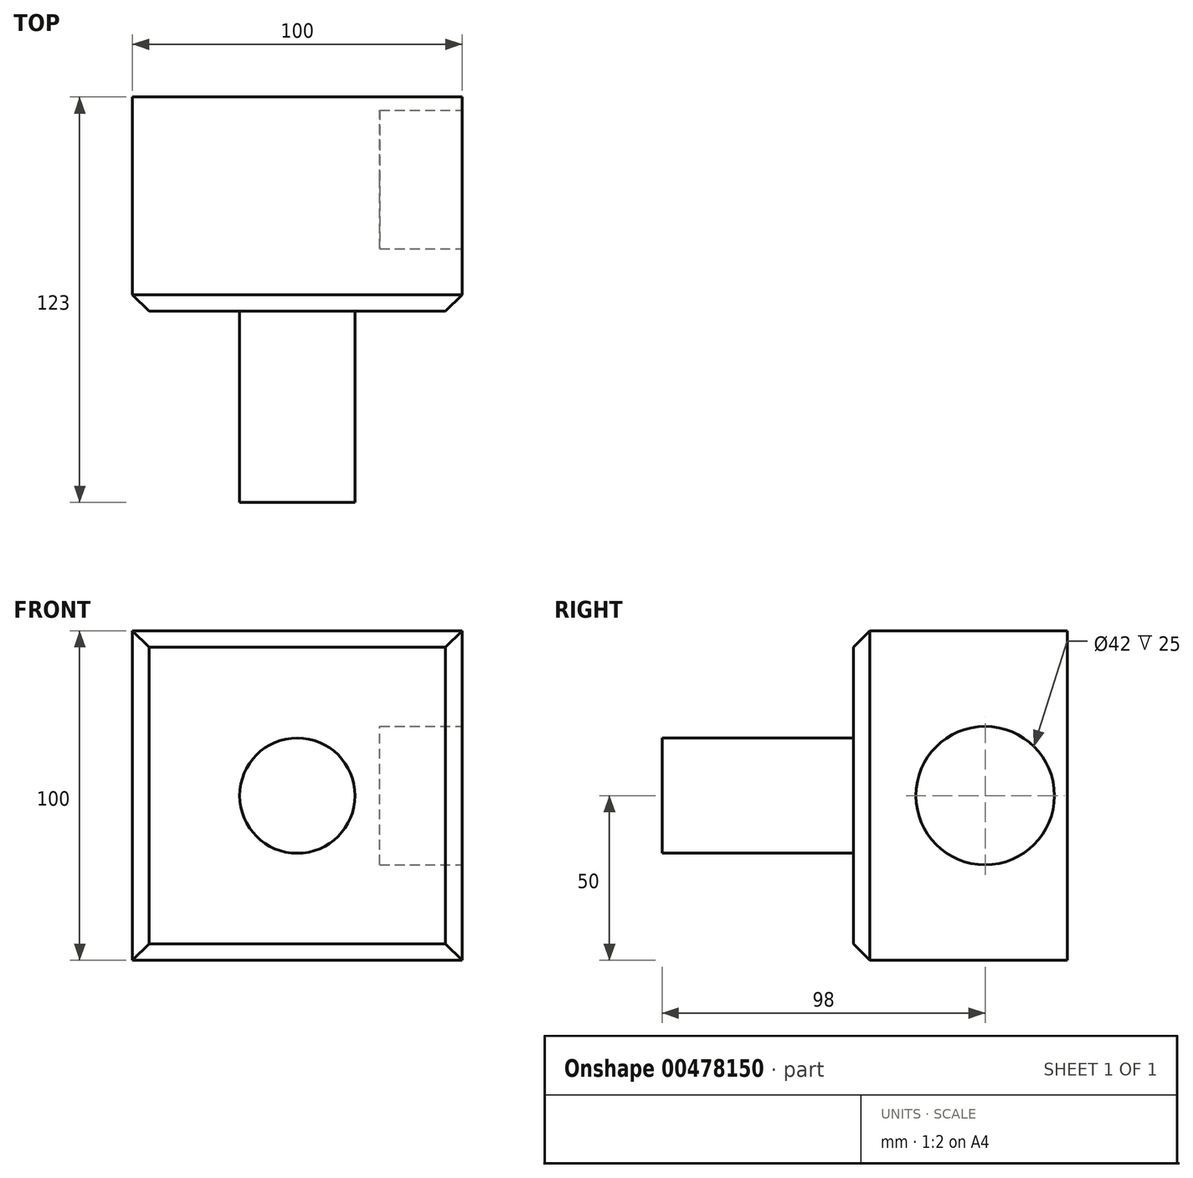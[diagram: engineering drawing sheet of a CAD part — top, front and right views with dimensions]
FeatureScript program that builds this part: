
annotation { "Feature Type Name" : "Feature", "Feature Type Description" : "" }
export const myFeature = defineFeature(function(context is Context, id is Id, definition is map)
    precondition{}
    {
        {
            var Q0;
            Q0=qCreatedBy(makeId("Front.planeOp"),FACE);
            var sketch = newSketch(context, id + "F0", { "sketchPlane" : qUnion([Q0])});
            skLineSegment(sketch, "E0.bottom", {"start": v(-50, 50) * mm, "end": v(50, 50) * mm});
            skLineSegment(sketch, "E0.top", {"start": v(-50, -50) * mm, "end": v(50, -50) * mm});
            skLineSegment(sketch, "E0.left", {"start": v(-50, 50) * mm, "end": v(-50, -50) * mm});
            skLineSegment(sketch, "E0.right", {"start": v(50, 50) * mm, "end": v(50, -50) * mm});
            skSolve(sketch);
        }
        {
            var Q0;
            Q0=makeQuery(id+"F0.imprint","IMPRINT",FACE,{"disambiguationData":[TD([[makeQuery(id+"F0.imprint","IMPRINT",EDGE,{"derivedFrom":sQuery(id+"F0.wireOp",EDGE,"E0.bottom")}),-1.0]])]});
            extrude(context, id + "F1", {"entities" : qUnion([Q0]), "depth" : 65 * mm});
        }
        {
            var Q0;
            Q0=makeQuery(id+"F1.opExtrude","CAP_FACE",FACE,{"disambiguationData":[OSD([sQuery(id+"F0.wireOp",EDGE,"E0.bottom"),sQuery(id+"F0.wireOp",EDGE,"E0.top"),sQuery(id+"F0.wireOp",EDGE,"E0.left"),sQuery(id+"F0.wireOp",EDGE,"E0.right")])],"isStart":false});
            var sketch = newSketch(context, id + "F2", { "sketchPlane" : qUnion([Q0])});
            skCircle(sketch, "E1", {"center": v(0, 0) * mm, "radius": 17.5 * mm});
            skSolve(sketch);
        }
        {
            var Q0;
            Q0=makeQuery(id+"F2.imprint","IMPRINT",FACE,{"disambiguationData":[TD([[makeQuery(id+"F2.imprint","IMPRINT",EDGE,{"derivedFrom":sQuery(id+"F2.wireOp",EDGE,"E1")}),1.0]])]});
            extrude(context, id + "F3", {"entities" : qUnion([Q0]), "operationType" : NewBodyOperationType.ADD, "depth" : 58 * mm});
        }
        {
            var Q0;
            Q0=makeQuery(id+"F1.opExtrude","CAP_EDGE",EDGE,{"disambiguationData":[OSD([sQuery(id+"F0.wireOp",EDGE,"E0.right")])],"isStart":false});
            var Q1;
            Q1=makeQuery(id+"F1.opExtrude","CAP_EDGE",EDGE,{"disambiguationData":[OSD([sQuery(id+"F0.wireOp",EDGE,"E0.top")])],"isStart":false});
            var Q2;
            Q2=makeQuery(id+"F1.opExtrude","CAP_EDGE",EDGE,{"disambiguationData":[OSD([sQuery(id+"F0.wireOp",EDGE,"E0.bottom")])],"isStart":false});
            var Q3;
            Q3=makeQuery(id+"F1.opExtrude","CAP_EDGE",EDGE,{"disambiguationData":[OSD([sQuery(id+"F0.wireOp",EDGE,"E0.left")])],"isStart":false});
            chamfer(context, id + "F4", {"entities" : qUnion([Q0, Q1, Q2, Q3]), "width" : 5 * mm, "tangentPropagation" : true});
        }
        {
            var Q0;
            Q0=makeQuery(id+"F1.opExtrude","SWEPT_FACE",FACE,{"disambiguationData":[OSD([sQuery(id+"F0.wireOp",EDGE,"E0.right")])]});
            var sketch = newSketch(context, id + "F5", { "sketchPlane" : qUnion([Q0])});
            skCircle(sketch, "E2", {"center": v(-25, 0) * mm, "radius": 21 * mm});
            skSolve(sketch);
        }
        {
            var Q0;
            Q0=makeQuery(id+"F5.imprint","IMPRINT",FACE,{"disambiguationData":[TD([[makeQuery(id+"F5.imprint","IMPRINT",EDGE,{"derivedFrom":sQuery(id+"F5.wireOp",EDGE,"E2")}),1.0]])]});
            extrude(context, id + "F6", {"entities" : qUnion([Q0]), "operationType" : NewBodyOperationType.REMOVE, "oppositeDirection" : true, "depth" : 25 * mm});
        }
    });
